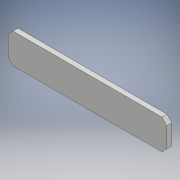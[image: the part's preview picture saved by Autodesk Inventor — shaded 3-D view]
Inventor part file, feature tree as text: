
AUTODESK INVENTOR PART (.ipt)
format: ipt  version: 2018 (Build 220112000, 112)  size: 98,304 bytes
history: native  units: mm
features: extrude x1, chamfer x1, sketch x1
ambient origin geometry x8: Origin, YZ Plane, XZ Plane, XY Plane, X Axis, Y Axis, Z Axis, Center Point
bodies: Solide1 (feature_tree)
feature tree (3):
  extrude  "Extrusion1"  Depth=18.0mm
  chamfer  "Chanfrein1"  Distance=95.0mm
  sketch  "Esquisse1"
